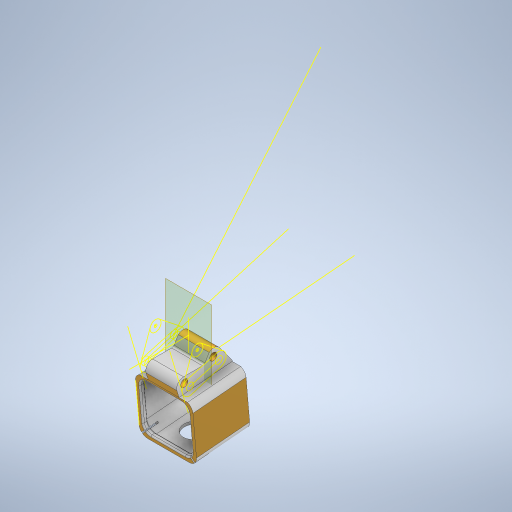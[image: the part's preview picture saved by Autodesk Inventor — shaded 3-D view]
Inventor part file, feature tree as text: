
AUTODESK INVENTOR PART (.ipt)
format: ipt  version: 2023 (Build 270158000, 158)  size: 853,504 bytes
history: native  units: in
note: dims shown in document units (in); Inventor stores cm internally (conversion verified against a paired STEP export)
features: sketch x10, projected_geometry x6, extrude x5, other x3, fillet x2, plane x1
ambient origin geometry x8: Origin, YZ Plane, XZ Plane, XY Plane, X Axis, Y Axis, Z Axis, Center Point
bodies: Solid1 (feature_tree)
feature tree (27):
  other  "45 deg with session mount for boolian.iam"
  other  "45 deg mini predator fixed mount.ipt:1"
  other  "V2 session mount 45deg block.ipt:1"
  extrude  "Extrusion1"  Depth=0.3937in TaperAngle=0.0deg
  extrude  "Extrusion2"  Depth=0.0906in
  extrude  "Extrusion3"  Depth=0.3937in TaperAngle=0.0deg
  extrude  "Extrusion4"  Depth=0.3937in TaperAngle=0.0deg
  extrude  "Extrusion5"  Depth=0.0787in
  fillet  "Fillet1"  [1 undecoded]
  fillet  "Fillet2"  [1 undecoded]
  sketch  "Sketch18"
  sketch  "Sketch2"  dims[d3=1.0in d4=0.0in d6=0.0906in]
  sketch  "Sketch2_1"  dims[d0=0.3937in d1=1.0in d2=0.0in]
  plane  "Work Plane1"
  sketch  "Sketch6"  dims[d7=0.0906in d8=0.3937in d9=0.0in]
  sketch  "Sketch7"  dims[d10=0.3937in d11=0.0in d12=0.3937in d13=0.0in]
  sketch  "Sketch8"  dims[d14=0.1969in d15=0.0787in]
  projected_geometry  "Projected Loop1"
  sketch  "Sketch9"
  projected_geometry  "Projected Loop2"
  sketch  "Sketch10"
  projected_geometry  "Projected Loop3"
  projected_geometry  "Projected Loop4"
  projected_geometry  "Projected Loop5"
  sketch  "Sketch11"
  projected_geometry  "Projected Loop6"
  sketch  "Sketch12"
note: 2 required parameter values undecoded (feature->parameter linkage not recoverable at this tier; creation-order binding heuristic only, values carry confidence <= 0.55)
